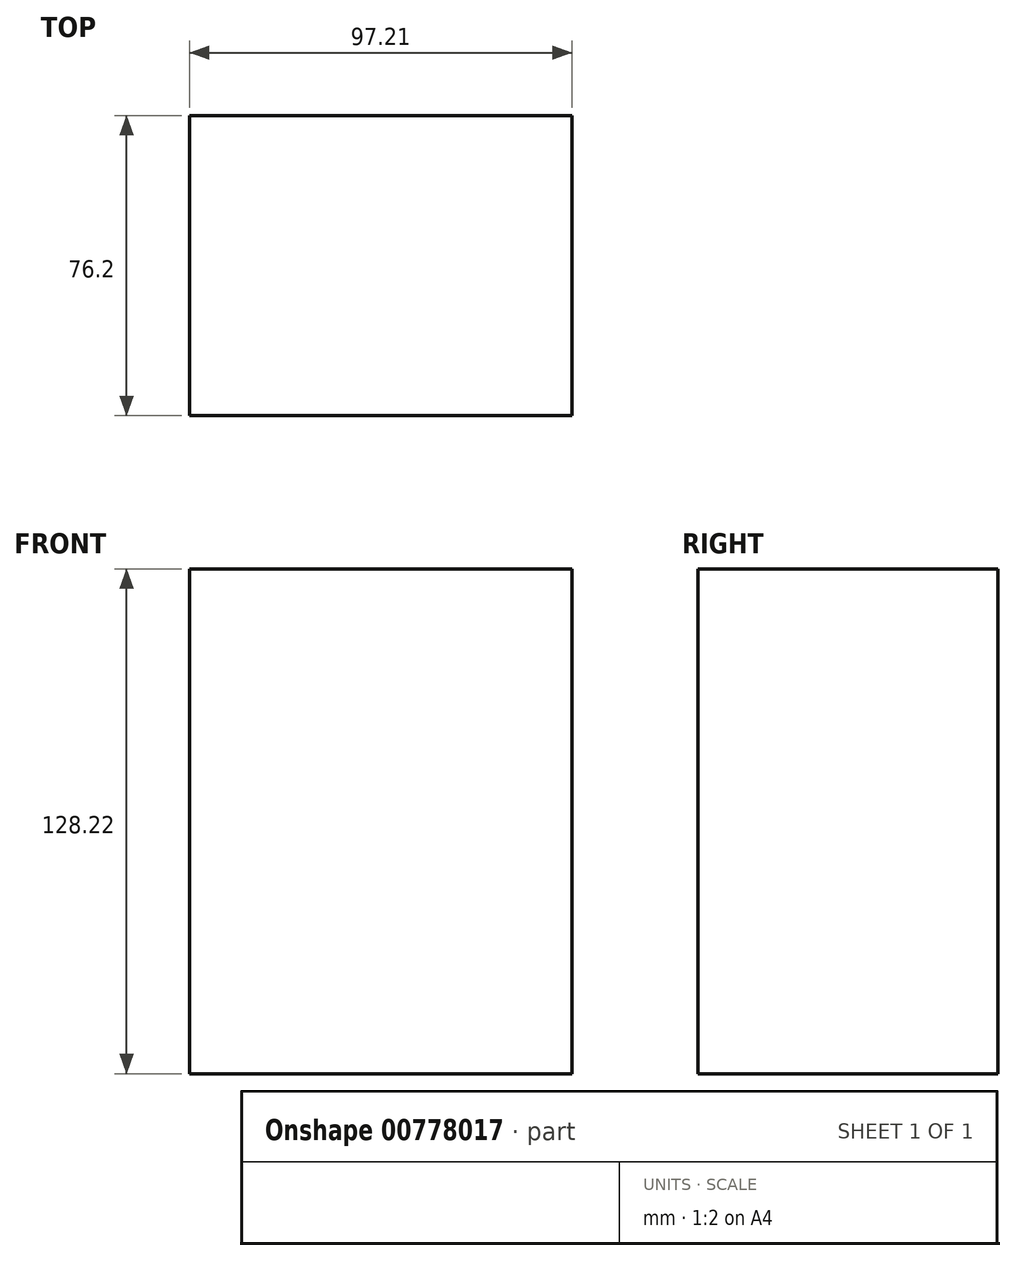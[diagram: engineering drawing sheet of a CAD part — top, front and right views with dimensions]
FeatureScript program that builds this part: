
annotation { "Feature Type Name" : "Feature", "Feature Type Description" : "" }
export const myFeature = defineFeature(function(context is Context, id is Id, definition is map)
    precondition{}
    {
        {
            var Q0;
            Q0=qCreatedBy(makeId("Front.planeOp"),FACE);
            var sketch = newSketch(context, id + "F0", { "sketchPlane" : qUnion([Q0])});
            skLineSegment(sketch, "E0.bottom", {"start": v(-46.87, 71.48) * mm, "end": v(50.34, 71.48) * mm});
            skLineSegment(sketch, "E0.top", {"start": v(-46.87, -56.74) * mm, "end": v(50.34, -56.74) * mm});
            skLineSegment(sketch, "E0.left", {"start": v(-46.87, 71.48) * mm, "end": v(-46.87, -56.74) * mm});
            skLineSegment(sketch, "E0.right", {"start": v(50.34, 71.48) * mm, "end": v(50.34, -56.74) * mm});
            skLineSegment(sketch, "E1.bottom", {"start": v(50.34, 71.48) * mm, "end": v(-46.87, 71.48) * mm});
            skLineSegment(sketch, "E1.top", {"start": v(50.34, -56.74) * mm, "end": v(-46.87, -56.74) * mm});
            skSolve(sketch);
        }
        {
            var Q0;
            Q0 = qSketchRegion(id + "F0", true);
            extrude(context, id + "F1", {"entities" : qUnion([Q0]), "depth" : 76.2 * mm, "offsetDistance" : 25.4 * mm});
        }
    });
